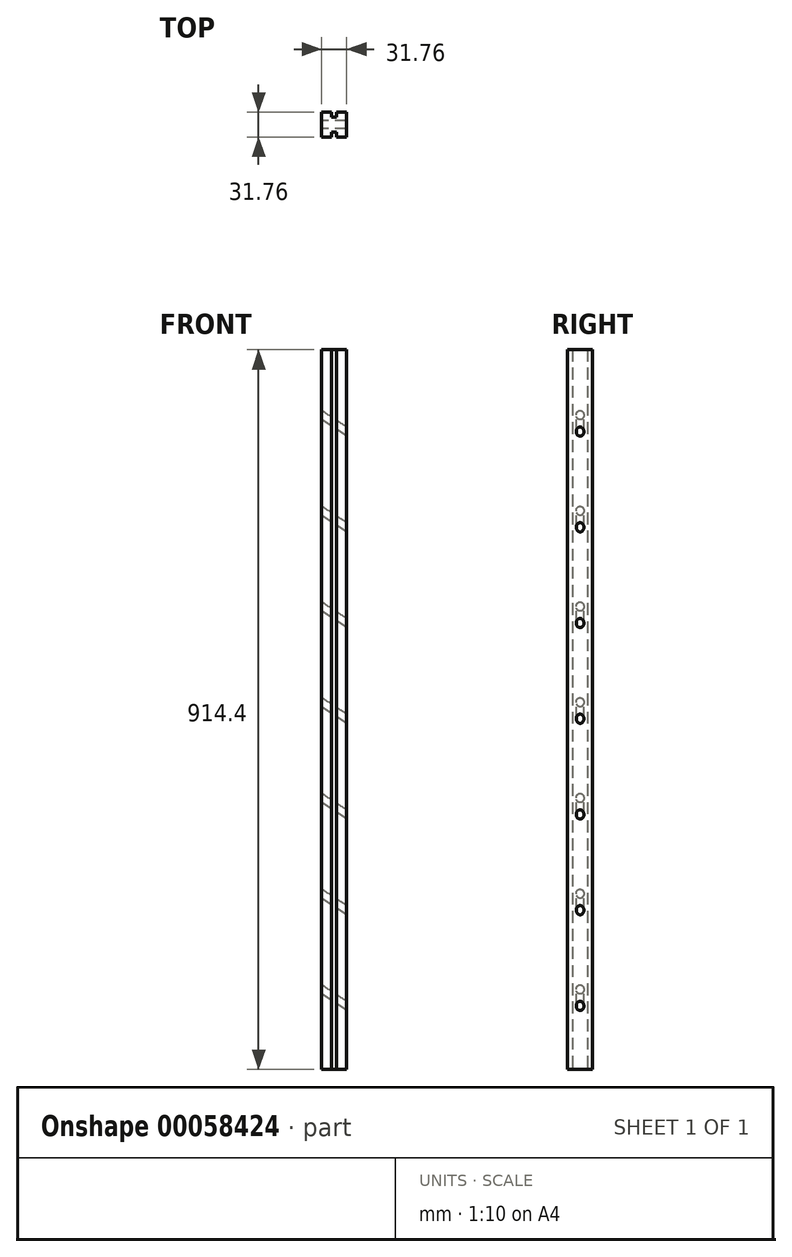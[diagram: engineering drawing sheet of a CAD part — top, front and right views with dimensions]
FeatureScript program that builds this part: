
annotation { "Feature Type Name" : "Feature", "Feature Type Description" : "" }
export const myFeature = defineFeature(function(context is Context, id is Id, definition is map)
    precondition{}
    {
        {
            var Q0;
            Q0=qCreatedBy(makeId("Top.planeOp"),FACE);
            var sketch = newSketch(context, id + "F0", { "sketchPlane" : qUnion([Q0])});
            skLineSegment(sketch, "E0.rect.bottom", {"start": v(15.88, -15.87) * mm, "end": v(3.18, -15.88) * mm});
            skLineSegment(sketch, "E0.rect.top", {"start": v(15.87, 15.88) * mm, "end": v(3.17, 15.87) * mm});
            skLineSegment(sketch, "E0.rect.left", {"start": v(15.88, -15.87) * mm, "end": v(15.87, 15.88) * mm});
            skLineSegment(sketch, "E0.rect.right", {"start": v(-15.87, -15.88) * mm, "end": v(-15.88, 15.87) * mm});
            skPoint(sketch, "E0.rect.middle", {"position": v(0, 0) * mm});
            skLineSegment(sketch, "E1", {"start": v(-3.18, 15.87) * mm, "end": v(-3.18, 9.52) * mm});
            skLineSegment(sketch, "E2", {"start": v(-3.18, 9.52) * mm, "end": v(3.17, 9.52) * mm});
            skLineSegment(sketch, "E3", {"start": v(3.17, 9.52) * mm, "end": v(3.17, 15.87) * mm});
            skLineSegment(sketch, "E4", {"start": v(-3.17, -15.88) * mm, "end": v(-3.17, -9.53) * mm});
            skLineSegment(sketch, "E5", {"start": v(-3.17, -9.53) * mm, "end": v(3.18, -9.52) * mm});
            skLineSegment(sketch, "E6", {"start": v(3.18, -9.53) * mm, "end": v(3.18, -15.88) * mm});
            skLineSegment(sketch, "E7", {"start": v(0, 9.52) * mm, "end": v(0, -9.53) * mm, "construction": true});
            skLineSegment(sketch, "E8.trimOffspring", {"start": v(-3.18, 15.87) * mm, "end": v(-15.88, 15.87) * mm});
            skLineSegment(sketch, "E9.trimOffspring", {"start": v(-3.17, -15.88) * mm, "end": v(-15.87, -15.88) * mm});
            skSolve(sketch);
        }
        {
            var Q0;
            Q0=qSketchRegion(id+"F0",true);
            extrude(context, id + "F1", {"entities" : qUnion([Q0]), "depth" : 914.4 * mm});
        }
        {
            var Q0;
            Q0=makeQuery(id+"F1.opExtrude","SWEPT_FACE",FACE,{"disambiguationData":[OSD([sQuery(id+"F0.wireOp",EDGE,"E0.rect.right")])]});
            var Q1;
            Q1=makeQuery(id+"F1.opExtrude","CAP_EDGE",EDGE,{"disambiguationData":[OSD([sQuery(id+"F0.wireOp",EDGE,"E0.rect.right")])],"isStart":false});
            cPlane(context, id + "F2", {"entities" : qUnion([Q0, Q1]), "cplaneType" : CPlaneType.LINE_ANGLE, "offset" : 152.4 * mm, "angle" : 33.33 * degree, "width" : 152.4 * mm, "height" : 152.4 * mm});
        }
        {
            var Q0;
            Q0=qCreatedBy(id+"F2.planeOp",FACE);
            var sketch = newSketch(context, id + "F3", { "sketchPlane" : qUnion([Q0])});
            skLineSegment(sketch, "E10", {"start": v(0, 0) * mm, "end": v(0, 755.28) * mm, "construction": true});
            skCircle(sketch, "E11", {"center": v(0, 787.4) * mm, "radius": 4.89 * mm});
            skCircle(sketch, "E12", {"center": v(0, 685.8) * mm, "radius": 4.89 * mm});
            skCircle(sketch, "E13", {"center": v(0, 584.2) * mm, "radius": 4.89 * mm});
            skCircle(sketch, "E14", {"center": v(0, 482.6) * mm, "radius": 4.89 * mm});
            skCircle(sketch, "E15", {"center": v(0, 381) * mm, "radius": 4.89 * mm});
            skCircle(sketch, "E16", {"center": v(0, 279.4) * mm, "radius": 4.89 * mm});
            skCircle(sketch, "E17", {"center": v(0, 177.8) * mm, "radius": 4.89 * mm});
            skCircle(sketch, "E18", {"center": v(0, 76.2) * mm, "radius": 4.89 * mm});
            skSolve(sketch);
        }
        {
            var Q0;
            Q0=qSketchRegion(id+"F3",true);
            extrude(context, id + "F4", {"entities" : qUnion([Q0]), "operationType" : NewBodyOperationType.REMOVE, "endBound" : BoundingType.THROUGH_ALL, "depth" : 25.4 * mm});
        }
    });
